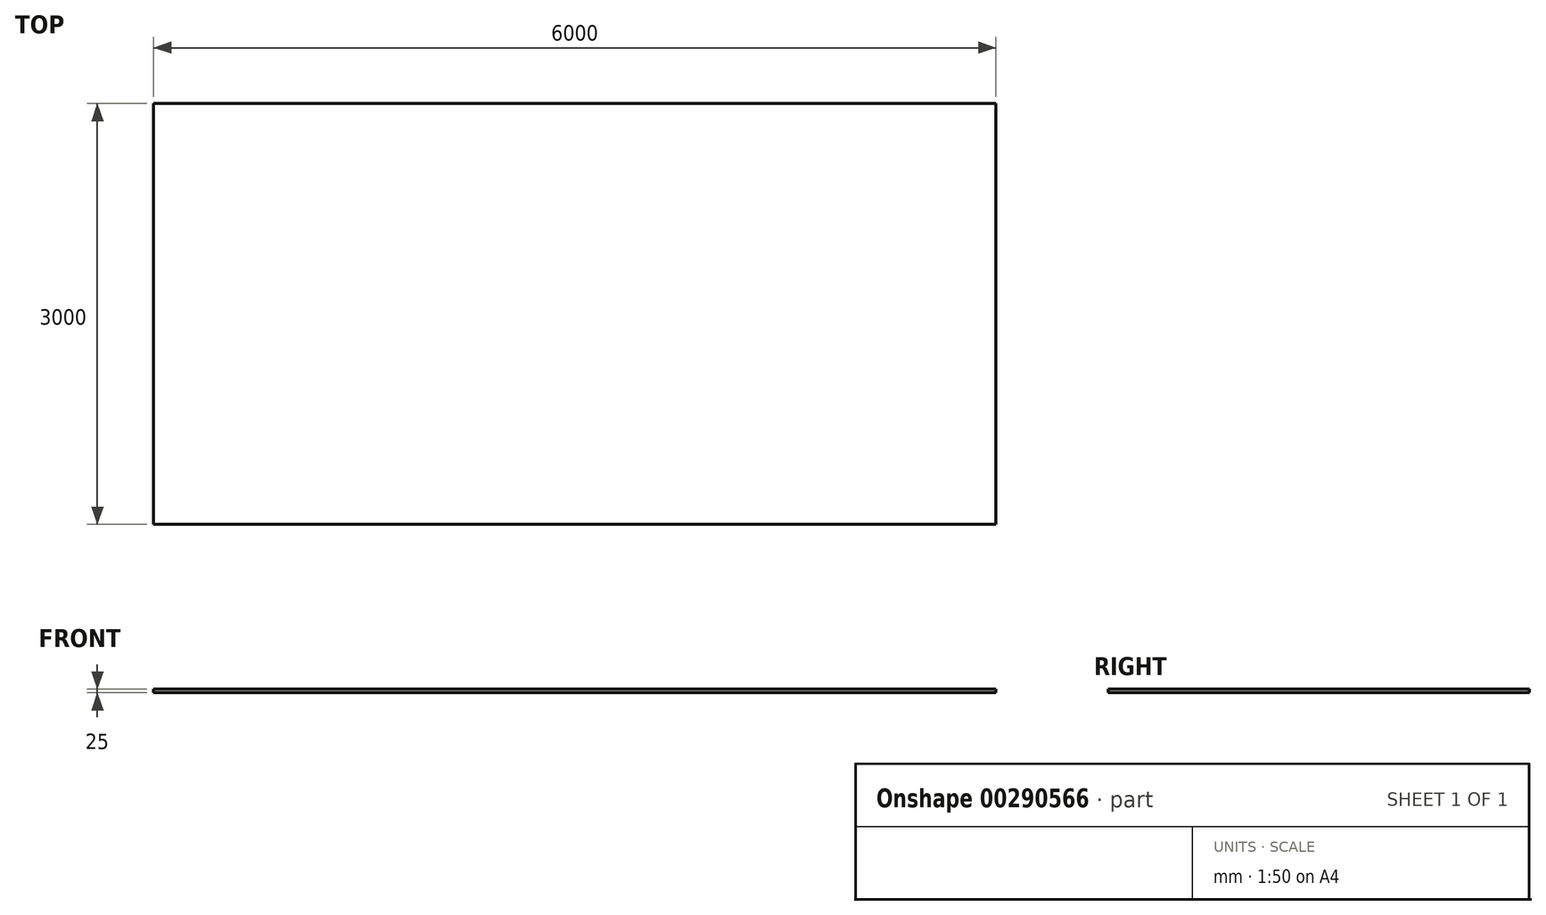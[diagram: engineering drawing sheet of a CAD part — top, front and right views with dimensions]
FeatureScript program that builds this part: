
annotation { "Feature Type Name" : "Feature", "Feature Type Description" : "" }
export const myFeature = defineFeature(function(context is Context, id is Id, definition is map)
    precondition{}
    {
        {
            var Q0;
            Q0=qCreatedBy(makeId("Top.planeOp"),FACE);
            var sketch = newSketch(context, id + "F0", { "sketchPlane" : qUnion([Q0])});
            skLineSegment(sketch, "E0.bottom", {"start": v(-3000, 1500) * mm, "end": v(3000, 1500) * mm});
            skLineSegment(sketch, "E0.top", {"start": v(-3000, -1500) * mm, "end": v(3000, -1500) * mm});
            skLineSegment(sketch, "E0.left", {"start": v(-3000, 1500) * mm, "end": v(-3000, -1500) * mm});
            skLineSegment(sketch, "E0.right", {"start": v(3000, 1500) * mm, "end": v(3000, -1500) * mm});
            skPoint(sketch, "E0.middle", {"position": v(0, 0) * mm});
            skSolve(sketch);
        }
        {
            var Q0;
            Q0 = qSketchRegion(id + "F0", true);
            extrude(context, id + "F1", {"entities" : qUnion([Q0]), "depth" : 25 * mm});
        }
    });
